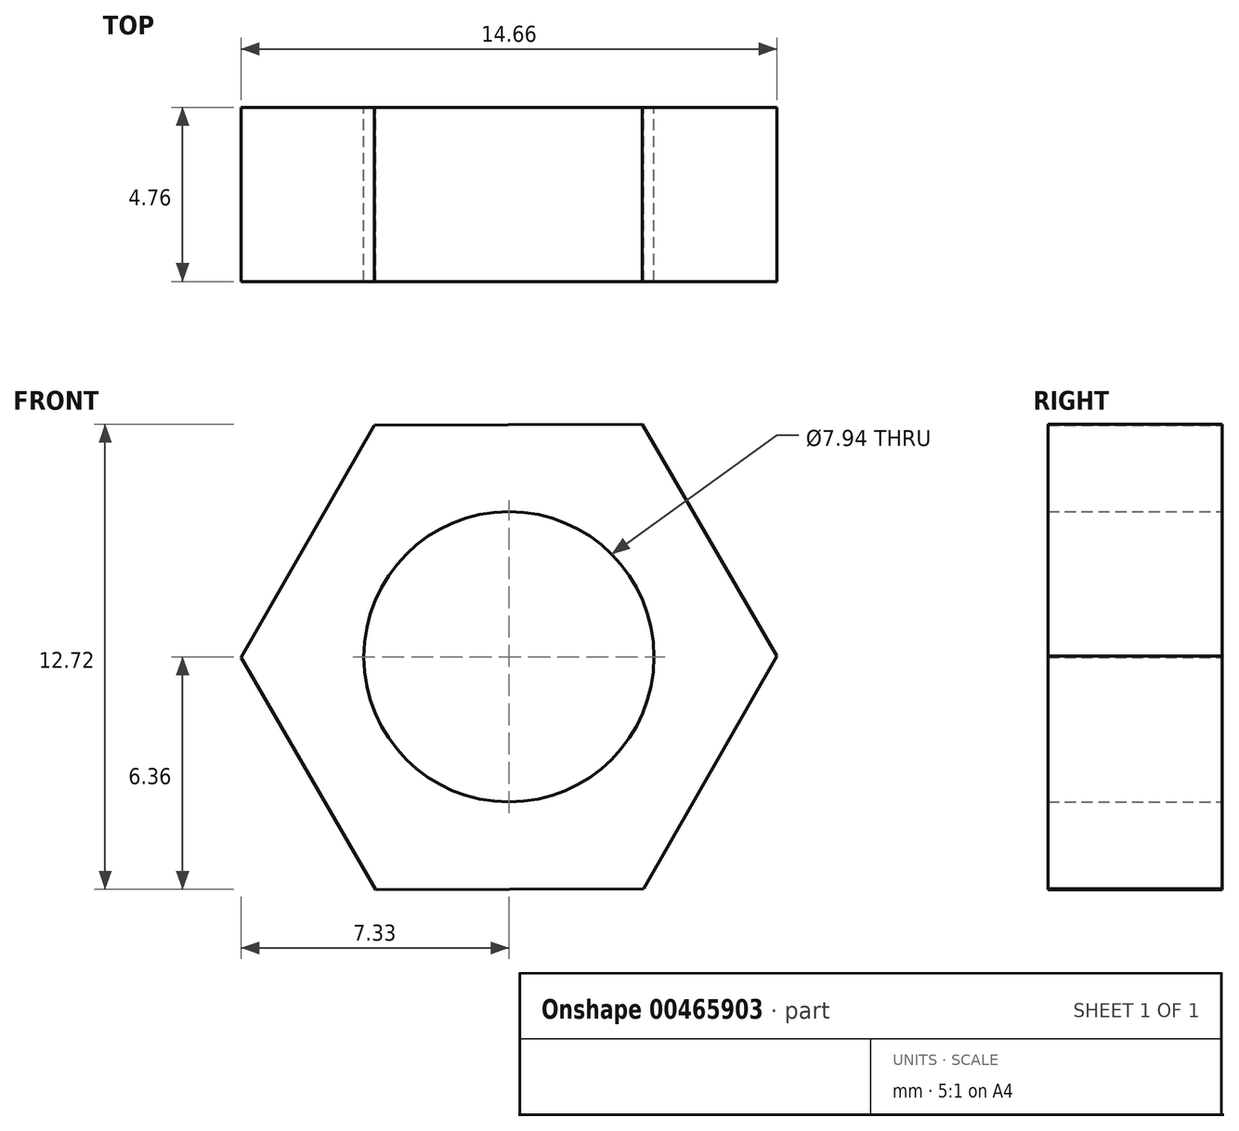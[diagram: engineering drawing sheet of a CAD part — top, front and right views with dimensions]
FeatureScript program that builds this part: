
annotation { "Feature Type Name" : "Feature", "Feature Type Description" : "" }
export const myFeature = defineFeature(function(context is Context, id is Id, definition is map)
    precondition{}
    {
        {
            var Q0;
            Q0=qCreatedBy(makeId("Front.planeOp"),FACE);
            var sketch = newSketch(context, id + "F0", { "sketchPlane" : qUnion([Q0])});
            skCircle(sketch, "E0", {"center": v(0, 0) * mm, "radius": 3.97 * mm});
            skCircle(sketch, "E1", {"center": v(0, 0) * mm, "radius": 6.35 * mm});
            skCircle(sketch, "E2.cCircle", {"center": v(0, 0) * mm, "radius": 6.35 * mm, "construction": true});
            skLineSegment(sketch, "E2.0", {"start": v(-7.33, -0.02) * mm, "end": v(-3.69, 6.34) * mm});
            skLineSegment(sketch, "E2.1", {"start": v(-3.69, 6.34) * mm, "end": v(3.65, 6.36) * mm});
            skLineSegment(sketch, "E2.2", {"start": v(3.65, 6.36) * mm, "end": v(7.33, 0.02) * mm});
            skLineSegment(sketch, "E2.3", {"start": v(7.33, 0.02) * mm, "end": v(3.69, -6.34) * mm});
            skLineSegment(sketch, "E2.4", {"start": v(3.69, -6.34) * mm, "end": v(-3.65, -6.36) * mm});
            skLineSegment(sketch, "E2.5", {"start": v(-3.65, -6.36) * mm, "end": v(-7.33, -0.02) * mm});
            skPoint(sketch, "E2.0.midPoint", {"position": v(-5.5, 3.16) * mm});
            skSolve(sketch);
        }
        {
            var Q0;
            Q0=makeQuery(id+"F0.imprint","IMPRINT",FACE,{"disambiguationData":[TD([[makeQuery(id+"F0.imprint","IMPRINT",EDGE,{"derivedFrom":sQuery(id+"F0.wireOp",EDGE,"E0")}),-1.0]])]});
            var Q1;
            {var subQ0=sQuery(id+"F0.wireOp",EDGE,"E2.1");var subQ1=sQuery(id+"F0.wireOp",EDGE,"E1");var subQ2=makeQuery(id+"F0.imprint","INTERSECT",VERTEX,{"derivedFrom":[subQ1,subQ0]});Q1=makeQuery(id+"F0.imprint","IMPRINT",FACE,{"disambiguationData":[TD([[makeQuery(id+"F0.imprint","IMPRINT",EDGE,{"disambiguationData":[TD([[subQ2,-1.0]])],"derivedFrom":subQ1}),-1.0]])]});}
            var Q2;
            {var subQ0=sQuery(id+"F0.wireOp",EDGE,"E2.0");var subQ1=sQuery(id+"F0.wireOp",EDGE,"E1");var subQ2=makeQuery(id+"F0.imprint","INTERSECT",VERTEX,{"derivedFrom":[subQ1,subQ0]});Q2=makeQuery(id+"F0.imprint","IMPRINT",FACE,{"disambiguationData":[TD([[makeQuery(id+"F0.imprint","IMPRINT",EDGE,{"disambiguationData":[TD([[subQ2,-1.0]])],"derivedFrom":subQ1}),-1.0]])]});}
            var Q3;
            {var subQ0=sQuery(id+"F0.wireOp",EDGE,"E2.5");var subQ1=sQuery(id+"F0.wireOp",EDGE,"E1");var subQ2=makeQuery(id+"F0.imprint","INTERSECT",VERTEX,{"derivedFrom":[subQ1,subQ0]});Q3=makeQuery(id+"F0.imprint","IMPRINT",FACE,{"disambiguationData":[TD([[makeQuery(id+"F0.imprint","IMPRINT",EDGE,{"disambiguationData":[TD([[subQ2,-1.0]])],"derivedFrom":subQ1}),-1.0]])]});}
            var Q4;
            {var subQ0=sQuery(id+"F0.wireOp",EDGE,"E2.4");var subQ1=sQuery(id+"F0.wireOp",EDGE,"E1");var subQ2=makeQuery(id+"F0.imprint","INTERSECT",VERTEX,{"derivedFrom":[subQ1,subQ0]});Q4=makeQuery(id+"F0.imprint","IMPRINT",FACE,{"disambiguationData":[TD([[makeQuery(id+"F0.imprint","IMPRINT",EDGE,{"disambiguationData":[TD([[subQ2,-1.0]])],"derivedFrom":subQ1}),-1.0]])]});}
            var Q5;
            {var subQ0=sQuery(id+"F0.wireOp",EDGE,"E2.2");var subQ1=sQuery(id+"F0.wireOp",EDGE,"E1");var subQ2=makeQuery(id+"F0.imprint","INTERSECT",VERTEX,{"derivedFrom":[subQ1,subQ0]});Q5=makeQuery(id+"F0.imprint","IMPRINT",FACE,{"disambiguationData":[TD([[makeQuery(id+"F0.imprint","IMPRINT",EDGE,{"disambiguationData":[TD([[subQ2,1.0]])],"derivedFrom":subQ1}),-1.0]])]});}
            var Q6;
            {var subQ0=sQuery(id+"F0.wireOp",EDGE,"E2.1");var subQ1=sQuery(id+"F0.wireOp",EDGE,"E1");var subQ2=makeQuery(id+"F0.imprint","INTERSECT",VERTEX,{"derivedFrom":[subQ1,subQ0]});Q6=makeQuery(id+"F0.imprint","IMPRINT",FACE,{"disambiguationData":[TD([[makeQuery(id+"F0.imprint","IMPRINT",EDGE,{"disambiguationData":[TD([[subQ2,1.0]])],"derivedFrom":subQ1}),-1.0]])]});}
            extrude(context, id + "F1", {"entities" : qUnion([Q0, Q1, Q2, Q3, Q4, Q5, Q6]), "depth" : 4.76 * mm});
        }
    });
